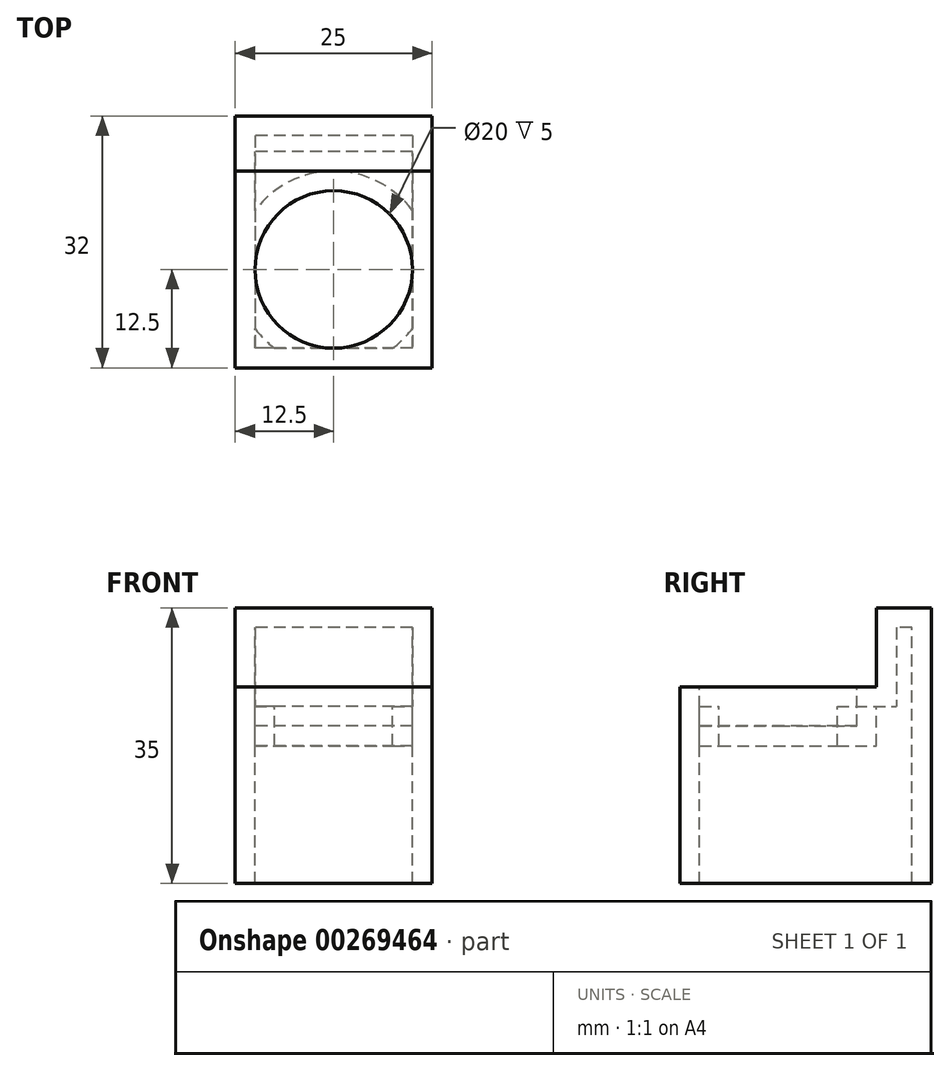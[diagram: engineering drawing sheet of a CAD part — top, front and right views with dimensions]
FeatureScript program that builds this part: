
annotation { "Feature Type Name" : "Feature", "Feature Type Description" : "" }
export const myFeature = defineFeature(function(context is Context, id is Id, definition is map)
    precondition{}
    {
        {
            var Q0;
            Q0=qCreatedBy(makeId("Right.planeOp"),FACE);
            var sketch = newSketch(context, id + "F0", { "sketchPlane" : qUnion([Q0])});
            skLineSegment(sketch, "E0.bottom", {"start": v(0, 0) * mm, "end": v(-32, 0) * mm});
            skLineSegment(sketch, "E0.top", {"start": v(0, 35) * mm, "end": v(-32, 35) * mm});
            skLineSegment(sketch, "E0.left", {"start": v(0, 0) * mm, "end": v(0, 35) * mm});
            skLineSegment(sketch, "E0.right", {"start": v(-32, 0) * mm, "end": v(-32, 35) * mm});
            skLineSegment(sketch, "E1", {"start": v(-32, 25) * mm, "end": v(0, 25) * mm});
            skLineSegment(sketch, "E2", {"start": v(-7, 35) * mm, "end": v(-7, 25) * mm});
            skSolve(sketch);
        }
        {
            var Q0;
            {var subQ3=sQuery(id+"F0.wireOp",EDGE,"E2");Q0=makeQuery(id+"F0.imprint","IMPRINT",FACE,{"disambiguationData":[TD([[makeQuery(id+"F0.imprint","IMPRINT",EDGE,{"derivedFrom":subQ3}),1.0]])]});}
            var Q1;
            {var subQ4=sQuery(id+"F0.wireOp",EDGE,"E0.bottom");Q1=makeQuery(id+"F0.imprint","IMPRINT",FACE,{"disambiguationData":[TD([[makeQuery(id+"F0.imprint","IMPRINT",EDGE,{"derivedFrom":subQ4}),-1.0]])]});}
            extrude(context, id + "F1", {"entities" : qUnion([Q0, Q1]), "depth" : 25 * mm});
        }
        {
            var Q0;
            Q0=makeQuery(id+"F1.opExtrude","SWEPT_FACE",FACE,{"disambiguationData":[OSD([sQuery(id+"F0.wireOp",EDGE,"E1")])]});
            var sketch = newSketch(context, id + "F2", { "sketchPlane" : qUnion([Q0])});
            skPoint(sketch, "E3", {"position": v(12.5, -19.5) * mm});
            skCircle(sketch, "E4", {"center": v(12.5, -19.5) * mm, "radius": 10 * mm});
            skSolve(sketch);
        }
        {
            var Q0;
            Q0=makeQuery(id+"F2.imprint","IMPRINT",FACE,{"disambiguationData":[TD([[makeQuery(id+"F2.imprint","IMPRINT",EDGE,{"derivedFrom":sQuery(id+"F2.wireOp",EDGE,"E4")}),1.0]])]});
            extrude(context, id + "F3", {"entities" : qUnion([Q0]), "operationType" : NewBodyOperationType.REMOVE, "oppositeDirection" : true, "depth" : 5 * mm});
        }
        {
            var Q0;
            Q0=makeQuery(id+"F1.opExtrude","SWEPT_FACE",FACE,{"disambiguationData":[OSD([sQuery(id+"F0.wireOp",EDGE,"E0.bottom")])]});
            shell(context, id + "F4", {"entities" : qUnion([Q0]), "thickness" : 2.5 * mm});
        }
    });
